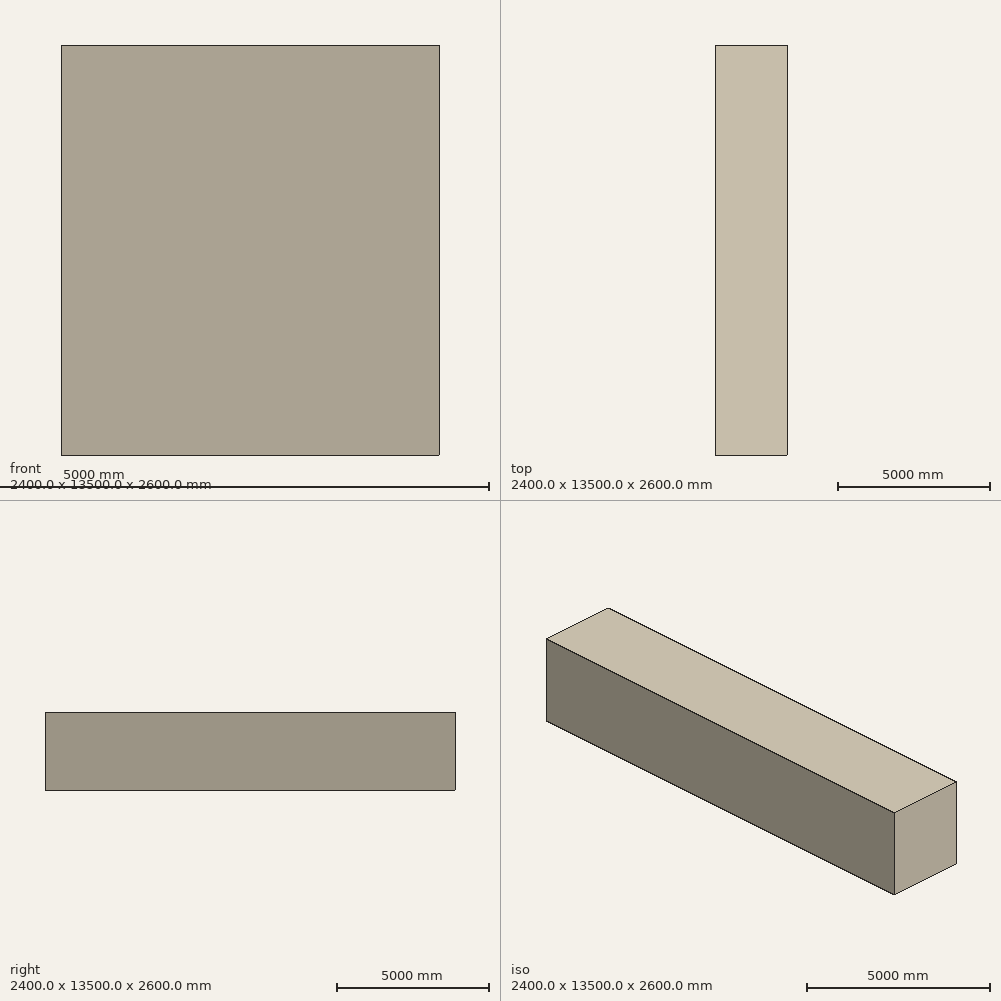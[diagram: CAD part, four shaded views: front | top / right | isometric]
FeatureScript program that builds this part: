
annotation { "Feature Type Name" : "Feature", "Feature Type Description" : "" }
export const myFeature = defineFeature(function(context is Context, id is Id, definition is map)
    precondition{}
    {
        {
            var Q0;
            Q0=qCreatedBy(makeId("Front.planeOp"),FACE);
            var sketch = newSketch(context, id + "F0", { "sketchPlane" : qUnion([Q0])});
            skLineSegment(sketch, "E0.bottom", {"start": v(0, 0) * mm, "end": v(2400, 0) * mm});
            skLineSegment(sketch, "E0.top", {"start": v(0, 2600) * mm, "end": v(2400, 2600) * mm});
            skLineSegment(sketch, "E0.left", {"start": v(0, 0) * mm, "end": v(0, 2600) * mm});
            skLineSegment(sketch, "E0.right", {"start": v(2400, 0) * mm, "end": v(2400, 2600) * mm});
            skSolve(sketch);
        }
        {
            var Q0;
            Q0=makeQuery(id+"F0.imprint","IMPRINT",FACE,{"disambiguationData":[TD([[makeQuery(id+"F0.imprint","IMPRINT",EDGE,{"derivedFrom":sQuery(id+"F0.wireOp",EDGE,"E0.bottom")}),1.0]])]});
            extrude(context, id + "F1", {"entities" : qUnion([Q0]), "depth" : 13500 * mm, "offsetDistance" : 25 * mm});
        }
    });
